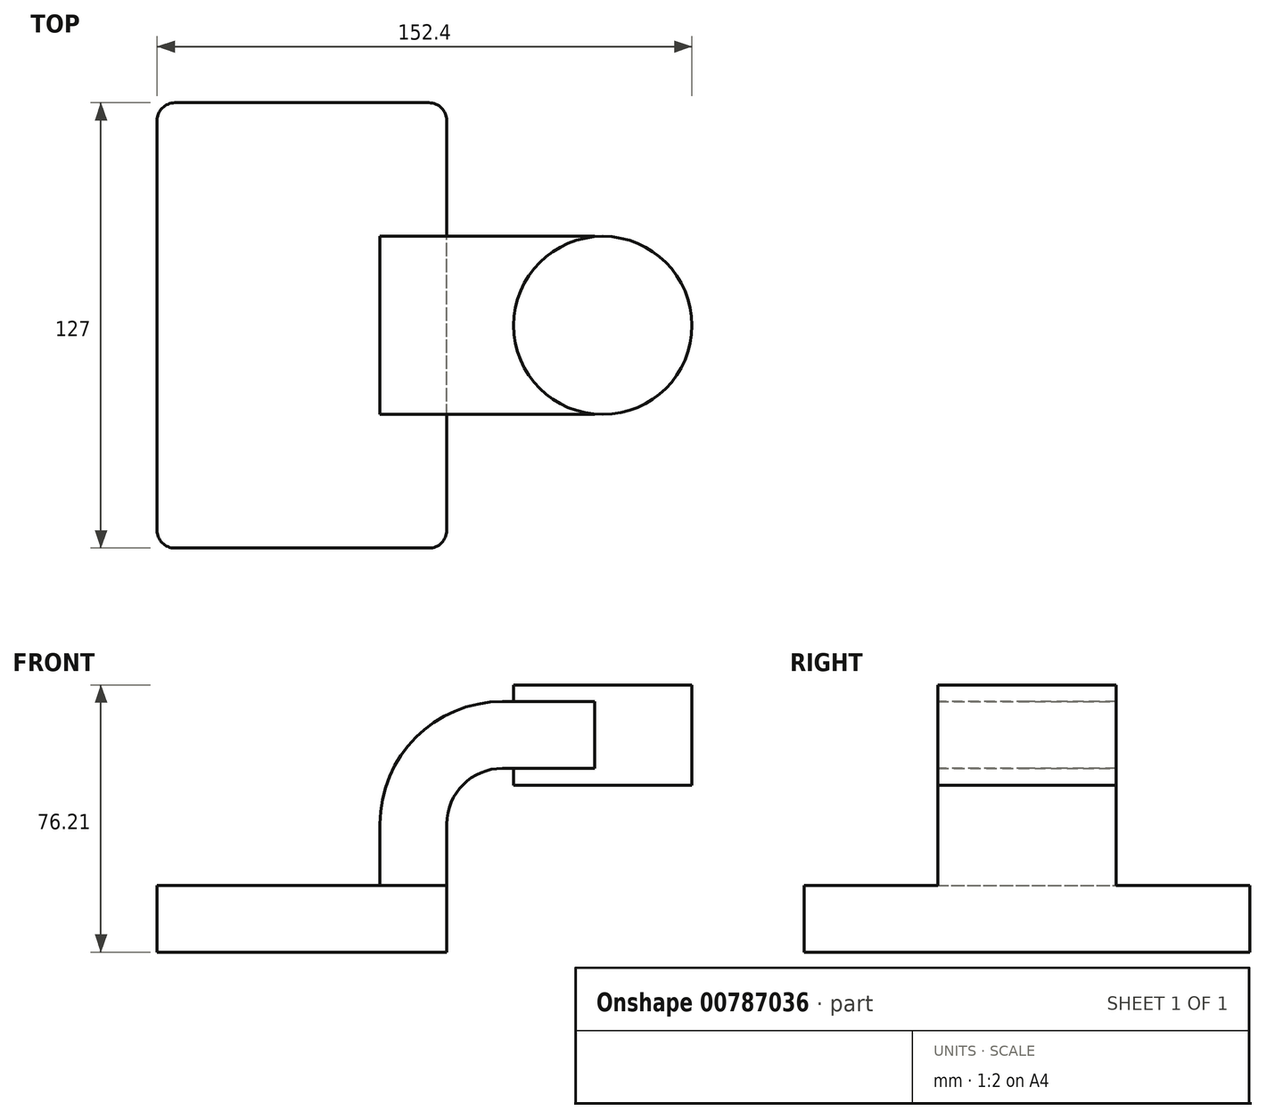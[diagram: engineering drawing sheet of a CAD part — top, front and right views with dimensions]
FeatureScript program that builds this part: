
annotation { "Feature Type Name" : "Feature", "Feature Type Description" : "" }
export const myFeature = defineFeature(function(context is Context, id is Id, definition is map)
    precondition{}
    {
        {
            var Q0;
            Q0=qCreatedBy(makeId("Front.planeOp"),FACE);
            var sketch = newSketch(context, id + "F0", { "sketchPlane" : qUnion([Q0])});
            skLineSegment(sketch, "E0.bottom", {"start": v(-41.28, -9.53) * mm, "end": v(41.28, -9.53) * mm});
            skLineSegment(sketch, "E0.top", {"start": v(-41.28, 9.53) * mm, "end": v(41.28, 9.53) * mm});
            skLineSegment(sketch, "E0.left", {"start": v(-41.28, -9.53) * mm, "end": v(-41.28, 9.53) * mm});
            skLineSegment(sketch, "E0.right", {"start": v(41.28, -9.53) * mm, "end": v(41.28, 9.53) * mm});
            skPoint(sketch, "E0.middle", {"position": v(0, 0) * mm});
            skLineSegment(sketch, "E1.bottom", {"start": v(60.33, 38.1) * mm, "end": v(111.12, 38.1) * mm});
            skLineSegment(sketch, "E1.top", {"start": v(60.33, 66.67) * mm, "end": v(111.12, 66.67) * mm});
            skLineSegment(sketch, "E1.left", {"start": v(60.33, 38.1) * mm, "end": v(60.33, 66.67) * mm});
            skLineSegment(sketch, "E1.right", {"start": v(111.12, 38.1) * mm, "end": v(111.12, 66.67) * mm});
            skPoint(sketch, "E1.middle", {"position": v(85.72, 52.39) * mm});
            skLineSegment(sketch, "E2", {"start": v(41.27, 9.53) * mm, "end": v(41.27, 27) * mm});
            skArc(sketch, "E3", {"start": v(41.27, 27) * mm, "mid": v(45.92, 38.23) * mm, "end": v(57.15, 42.88) * mm});
            skLineSegment(sketch, "E4", {"start": v(57.15, 42.88) * mm, "end": v(83.35, 42.88) * mm});
            skLineSegment(sketch, "E5.0", {"start": v(57.15, 61.93) * mm, "end": v(83.35, 61.93) * mm});
            skArc(sketch, "E5.1", {"start": v(22.23, 27) * mm, "mid": v(32.45, 51.7) * mm, "end": v(57.15, 61.93) * mm});
            skLineSegment(sketch, "E5.2", {"start": v(22.22, 9.53) * mm, "end": v(22.22, 27) * mm});
            skLineSegment(sketch, "E6", {"start": v(83.35, 42.88) * mm, "end": v(83.35, 61.93) * mm});
            skFitSpline(sketch, "E7", {"points": [v(-41.28, 9.53) * mm, v(57.15, 61.93) * mm], "startDerivative": vector(15.49, 106.03) * mm, "endDerivative": vector(123.45, -18.72) * mm});
            skLineSegment(sketch, "E8", {"start": v(85.72, 52.39) * mm, "end": v(85.72, 38.1) * mm});
            skLineSegment(sketch, "E9", {"start": v(85.72, 38.1) * mm, "end": v(85.72, 52.39) * mm});
            skLineSegment(sketch, "E10", {"start": v(85.72, 52.39) * mm, "end": v(85.72, 66.67) * mm});
            skSolve(sketch);
        }
        {
            var Q0;
            Q0=makeQuery(id+"F0.imprint","IMPRINT",FACE,{"disambiguationData":[TD([[makeQuery(id+"F0.imprint","IMPRINT",EDGE,{"derivedFrom":sQuery(id+"F0.wireOp",EDGE,"E0.bottom")}),1.0]])]});
            extrude(context, id + "F1", {"entities" : qUnion([Q0]), "endBound" : BoundingType.SYMMETRIC, "depth" : 127 * mm, "offsetDistance" : 25.4 * mm});
        }
        {
            var Q0;
            {var subQ5=sQuery(id+"F0.wireOp",EDGE,"E6");Q0=makeQuery(id+"F0.imprint","IMPRINT",FACE,{"disambiguationData":[TD([[makeQuery(id+"F0.imprint","IMPRINT",EDGE,{"derivedFrom":subQ5}),1.0]])]});}
            var Q1;
            {var subQ0=sQuery(id+"F0.wireOp",EDGE,"E2");Q1=makeQuery(id+"F0.imprint","IMPRINT",FACE,{"disambiguationData":[TD([[makeQuery(id+"F0.imprint","IMPRINT",EDGE,{"derivedFrom":subQ0}),1.0]])]});}
            extrude(context, id + "F2", {"entities" : qUnion([Q0, Q1]), "operationType" : NewBodyOperationType.ADD, "endBound" : BoundingType.SYMMETRIC, "depth" : 50.8 * mm, "offsetDistance" : 25.4 * mm});
        }
        {
            var Q0;
            Q0=makeQuery(id+"F0.imprint","IMPRINT",FACE,{"disambiguationData":[TD([[makeQuery(id+"F0.imprint","IMPRINT",EDGE,{"derivedFrom":sQuery(id+"F0.wireOp",EDGE,"E5.1")}),1.0]])]});
            extrude(context, id + "F3", {"entities" : qUnion([Q0]), "operationType" : NewBodyOperationType.ADD, "endBound" : BoundingType.SYMMETRIC, "depth" : 15.88 * mm, "offsetDistance" : 25.4 * mm});
        }
        {
            var Q0;
            {var subQ0=sQuery(id+"F0.wireOp",EDGE,"E1.right");Q0=makeQuery(id+"F0.imprint","IMPRINT",FACE,{"disambiguationData":[TD([[makeQuery(id+"F0.imprint","IMPRINT",EDGE,{"derivedFrom":subQ0}),1.0]])]});}
            var Q1;
            Q1=sQuery(id+"F0.wireOp",EDGE,"E9");
            revolve(context, id + "F4", {"operationType" : NewBodyOperationType.ADD, "surfaceOperationType" : NewSurfaceOperationType.NEW, "entities" : qUnion([Q0]), "axis" : qUnion([Q1]), "revolveType" : RevolveType.FULL});
        }
        {
            var Q0;
            Q0=makeQuery(id+"F1.opExtrude","CAP_EDGE",EDGE,{"disambiguationData":[OSD([sQuery(id+"F0.wireOp",EDGE,"E0.left")])],"isStart":false});
            var Q1;
            Q1=makeQuery(id+"F1.opExtrude","CAP_EDGE",EDGE,{"disambiguationData":[OSD([sQuery(id+"F0.wireOp",EDGE,"E0.right")])],"isStart":false});
            var Q2;
            Q2=makeQuery(id+"F1.opExtrude","CAP_EDGE",EDGE,{"disambiguationData":[OSD([sQuery(id+"F0.wireOp",EDGE,"E0.right")])],"isStart":true});
            var Q3;
            Q3=makeQuery(id+"F1.opExtrude","CAP_EDGE",EDGE,{"disambiguationData":[OSD([sQuery(id+"F0.wireOp",EDGE,"E0.left")])],"isStart":true});
            fillet(context, id + "F5", {"entities" : qUnion([Q0, Q1, Q2, Q3]), "radius" : 5.08 * mm, "tangentPropagation" : true, "allowEdgeOverflow" : false});
        }
    });
